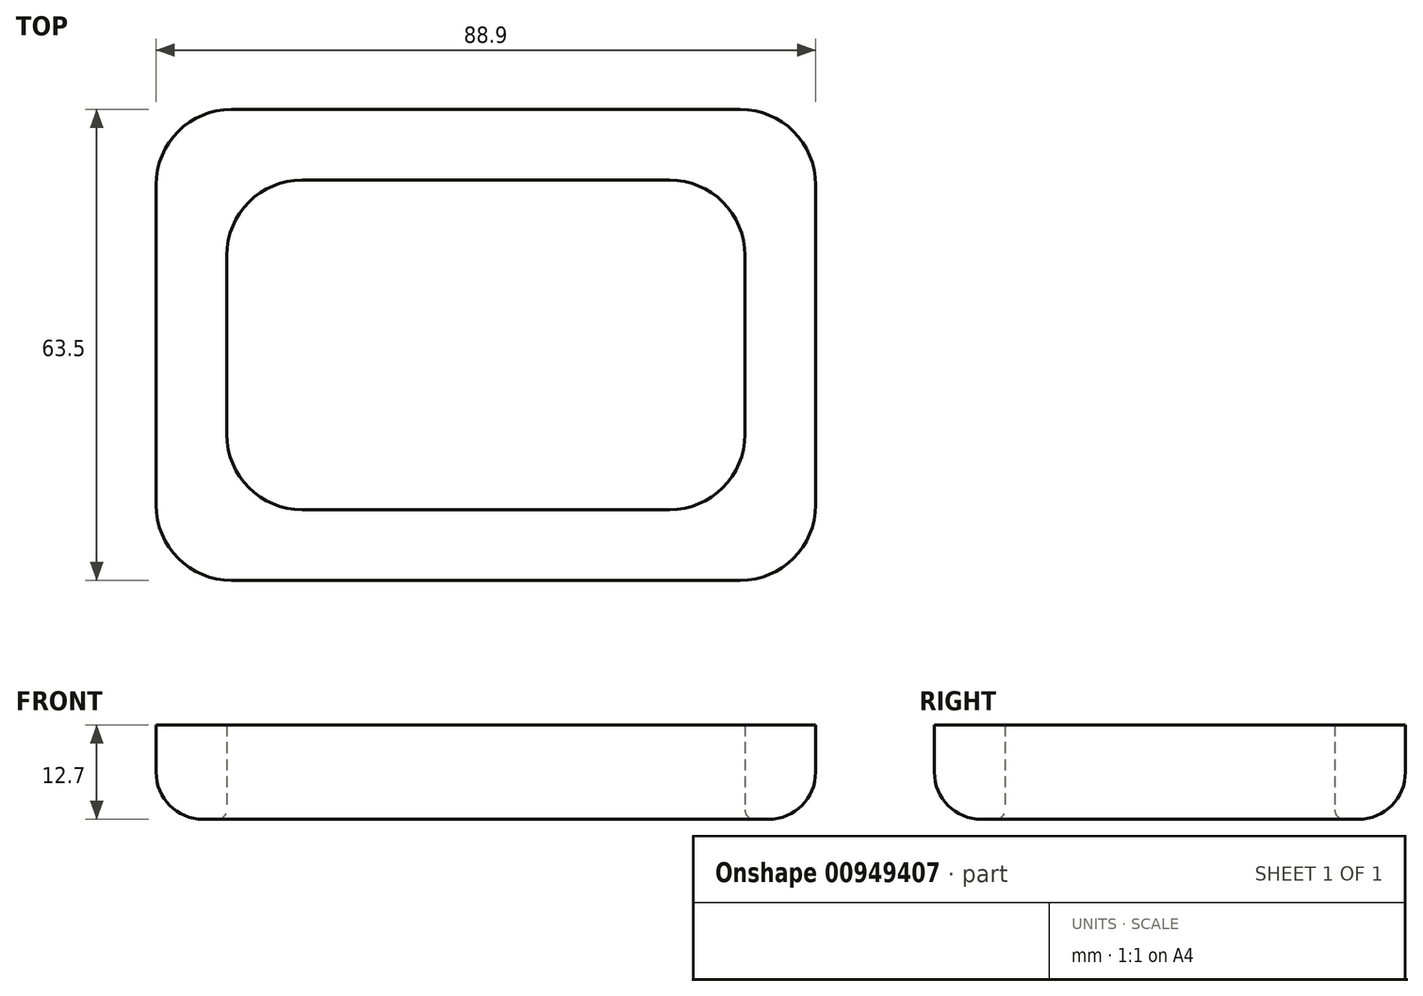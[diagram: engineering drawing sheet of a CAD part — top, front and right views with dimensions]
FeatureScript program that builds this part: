
annotation { "Feature Type Name" : "Feature", "Feature Type Description" : "" }
export const myFeature = defineFeature(function(context is Context, id is Id, definition is map)
    precondition{}
    {
        {
            var Q0;
            Q0=qCreatedBy(makeId("Top.planeOp"),FACE);
            var sketch = newSketch(context, id + "F0", { "sketchPlane" : qUnion([Q0])});
            skLineSegment(sketch, "E0.bottom", {"start": v(-34.3, 31.75) * mm, "end": v(34.29, 31.75) * mm});
            skLineSegment(sketch, "E0.top", {"start": v(-34.3, -31.75) * mm, "end": v(34.3, -31.75) * mm});
            skLineSegment(sketch, "E0.left", {"start": v(-44.45, 21.59) * mm, "end": v(-44.45, -21.6) * mm});
            skLineSegment(sketch, "E0.right", {"start": v(44.45, 21.6) * mm, "end": v(44.45, -21.6) * mm});
            skPoint(sketch, "E1.visualSharp", {"position": v(-44.45, 31.75) * mm});
            skArc(sketch, "E1.filletArc", {"start": v(-34.3, 31.75) * mm, "mid": v(-41.47, 28.77) * mm, "end": v(-44.45, 21.59) * mm});
            skPoint(sketch, "E2.visualSharp", {"position": v(-44.45, -31.75) * mm});
            skArc(sketch, "E2.filletArc", {"start": v(-44.45, -21.6) * mm, "mid": v(-41.47, -28.77) * mm, "end": v(-34.3, -31.75) * mm});
            skPoint(sketch, "E3.visualSharp", {"position": v(44.45, -31.75) * mm});
            skArc(sketch, "E3.filletArc", {"start": v(34.3, -31.75) * mm, "mid": v(41.47, -28.77) * mm, "end": v(44.45, -21.6) * mm});
            skPoint(sketch, "E4.visualSharp", {"position": v(44.45, 31.75) * mm});
            skArc(sketch, "E4.filletArc", {"start": v(44.45, 21.6) * mm, "mid": v(41.47, 28.77) * mm, "end": v(34.29, 31.75) * mm});
            skLineSegment(sketch, "E5.bottom", {"start": v(24.77, -22.23) * mm, "end": v(-24.76, -22.23) * mm});
            skLineSegment(sketch, "E5.top", {"start": v(24.77, 22.23) * mm, "end": v(-24.77, 22.23) * mm});
            skLineSegment(sketch, "E5.left", {"start": v(34.93, -12.06) * mm, "end": v(34.93, 12.07) * mm});
            skLineSegment(sketch, "E5.right", {"start": v(-34.92, -12.07) * mm, "end": v(-34.93, 12.07) * mm});
            skPoint(sketch, "E5.middle", {"position": v(0, 0) * mm});
            skPoint(sketch, "E6.visualSharp", {"position": v(-34.92, -22.23) * mm});
            skArc(sketch, "E6.filletArc", {"start": v(-34.92, -12.07) * mm, "mid": v(-31.95, -19.25) * mm, "end": v(-24.76, -22.23) * mm});
            skPoint(sketch, "E7.visualSharp", {"position": v(-34.93, 22.23) * mm});
            skArc(sketch, "E7.filletArc", {"start": v(-24.77, 22.23) * mm, "mid": v(-31.95, 19.25) * mm, "end": v(-34.93, 12.06) * mm});
            skPoint(sketch, "E8.visualSharp", {"position": v(34.92, 22.23) * mm});
            skArc(sketch, "E8.filletArc", {"start": v(34.92, 12.07) * mm, "mid": v(31.95, 19.25) * mm, "end": v(24.77, 22.23) * mm});
            skPoint(sketch, "E9.visualSharp", {"position": v(34.93, -22.23) * mm});
            skArc(sketch, "E9.filletArc", {"start": v(24.77, -22.23) * mm, "mid": v(31.95, -19.25) * mm, "end": v(34.93, -12.06) * mm});
            skSolve(sketch);
        }
        {
            var Q0;
            Q0=makeQuery(id+"F0.imprint","IMPRINT",FACE,{"disambiguationData":[TD([[makeQuery(id+"F0.imprint","IMPRINT",EDGE,{"derivedFrom":sQuery(id+"F0.wireOp",EDGE,"E0.bottom")}),-1.0]])]});
            extrude(context, id + "F1", {"entities" : qUnion([Q0]), "depth" : 12.7 * mm, "offsetDistance" : 25.4 * mm});
        }
        {
            var Q0;
            Q0=makeQuery(id+"F1.opExtrude","CAP_EDGE",EDGE,{"disambiguationData":[OSD([sQuery(id+"F0.wireOp",EDGE,"E2.filletArc")])],"isStart":true});
            fillet(context, id + "F2", {"entities" : qUnion([Q0]), "radius" : 6.35 * mm, "tangentPropagation" : true, "allowEdgeOverflow" : false});
        }
        {
            var Q0;
            Q0=makeQuery(id+"F1.opExtrude","CAP_EDGE",EDGE,{"disambiguationData":[OSD([sQuery(id+"F0.wireOp",EDGE,"E5.bottom")])],"isStart":true});
            var Q1;
            Q1=makeQuery(id+"F1.opExtrude","CAP_EDGE",EDGE,{"disambiguationData":[OSD([sQuery(id+"F0.wireOp",EDGE,"E6.filletArc")])],"isStart":true});
            var Q2;
            Q2=makeQuery(id+"F1.opExtrude","CAP_EDGE",EDGE,{"disambiguationData":[OSD([sQuery(id+"F0.wireOp",EDGE,"E5.right")])],"isStart":true});
            var Q3;
            Q3=makeQuery(id+"F1.opExtrude","CAP_EDGE",EDGE,{"disambiguationData":[OSD([sQuery(id+"F0.wireOp",EDGE,"E7.filletArc")])],"isStart":true});
            var Q4;
            Q4=makeQuery(id+"F1.opExtrude","CAP_EDGE",EDGE,{"disambiguationData":[OSD([sQuery(id+"F0.wireOp",EDGE,"E5.top")])],"isStart":true});
            var Q5;
            Q5=makeQuery(id+"F1.opExtrude","CAP_EDGE",EDGE,{"disambiguationData":[OSD([sQuery(id+"F0.wireOp",EDGE,"E8.filletArc")])],"isStart":true});
            var Q6;
            Q6=makeQuery(id+"F1.opExtrude","CAP_EDGE",EDGE,{"disambiguationData":[OSD([sQuery(id+"F0.wireOp",EDGE,"E5.left")])],"isStart":true});
            var Q7;
            Q7=makeQuery(id+"F1.opExtrude","CAP_EDGE",EDGE,{"disambiguationData":[OSD([sQuery(id+"F0.wireOp",EDGE,"E9.filletArc")])],"isStart":true});
            fillet(context, id + "F3", {"entities" : qUnion([Q0, Q1, Q2, Q3, Q4, Q5, Q6, Q7]), "radius" : 1.27 * mm, "tangentPropagation" : true, "allowEdgeOverflow" : false});
        }
    });
